# Revit family: DATABAR Single Outlet Tap Off Unit
name_source: partatom
category: Electrical Equipment
revit_build: Autodesk Revit 2018 (Build: 20190510_1515(x64)
units: mm (PartAtom-declared; Revit-internal decimal feet)

## family parameters
Cut with Voids When Loaded = No
Host = Face
OmniClass Number = 23.80.30.11.17
OmniClass Title = Distribution Boards and Control Panels
Panel Configuration = Two Columns, Circuits Across
Part Type = Panelboard
Room Calculation Point = No
Round Connector Dimension = Use Diameter
Shared = No

## types (15) — shared parameters
AMG_Tap_Off_Length = 210 mm  [stored 0.688976 ft]
AMG_Tap_Off_Socket_Height = 53 mm  [stored 0.173885 ft]
Default Elevation = 1219 mm
Manufacturer = Anord Mardix
Version = A

## per-type parameters (varying)
| type | AMG_Tap_Off_Height | AMG_Tap_Off_Width | Description |
| Single Outlet 16A - SP&Meter | 98 mm  [stored 0.321522 ft] | 165 mm | Tap Off Unit, Single Outlet, 16A, SP&Meter |
| Single Outlet 16A - TP | 98 mm  [stored 0.321522 ft] | 165 mm | Tap Off Unit, Single Outlet, 16A, TP |
| Single Outlet 16A - DP | 98 mm  [stored 0.321522 ft] | 165 mm | Tap Off Unit, Single Outlet, 16A, DP |
| Single Outlet 16A - SP | 98 mm  [stored 0.321522 ft] | 165 mm | Tap Off Unit, Single Outlet, 16A, SP |
| Single Outlet 32A - SP | 98 mm  [stored 0.321522 ft] | 165 mm | Tap Off Unit, Single Outlet, 32A, SP |
| Single Outlet 32A - DP | 98 mm  [stored 0.321522 ft] | 165 mm | Tap Off Unit, Single Outlet, 32A, DP |
| Single Outlet 32A - TP | 98 mm  [stored 0.321522 ft] | 165 mm | Tap Off Unit, Single Outlet, 32A, TP |
| Single Outlet 32A - SP&Meter | 98 mm  [stored 0.321522 ft] | 165 mm | Tap Off Unit, Single Outlet, 32A, SP&Meter |
| Single Outlet 16A - TP&Meter | 182 mm  [stored 0.597113 ft] | 165 mm | Tap Off Unit, Single Outlet, 16A, TP&Meter |
| Single Outlet 63A - SP | 98 mm  [stored 0.321522 ft] | 165 mm | Tap Off Unit, Single Outlet, 63A, SP |
| Single Outlet 32A - TP&Meter | 182 mm  [stored 0.597113 ft] | 159 mm  [stored 0.521654 ft] | Tap Off Unit, Single Outlet, 32A, TP&Meter |
| Single Outlet 63A - DP | 98 mm  [stored 0.321522 ft] | 165 mm | Tap Off Unit, Single Outlet, 63A, DP |
| Single Outlet 63A - TP | 98 mm  [stored 0.321522 ft] | 165 mm | Tap Off Unit, Single Outlet, 63A, TP |
| Single Outlet 63A - SP&Meter | 98 mm  [stored 0.321522 ft] | 165 mm | Tap Off Unit, Single Outlet, 63A, SP&Meter |
| Single Outlet 63A - TP&Meter | 182 mm  [stored 0.597113 ft] | 165 mm | Tap Off Unit, Single Outlet, 63A, TP&Meter |

note: [stored X ft] marks values corroborated as IEEE doubles in the binary element streams (Revit-internal decimal feet)

## geometry (parser evidence)
native form markers: Sweep x11
no freeform markers — native parametric forms only
